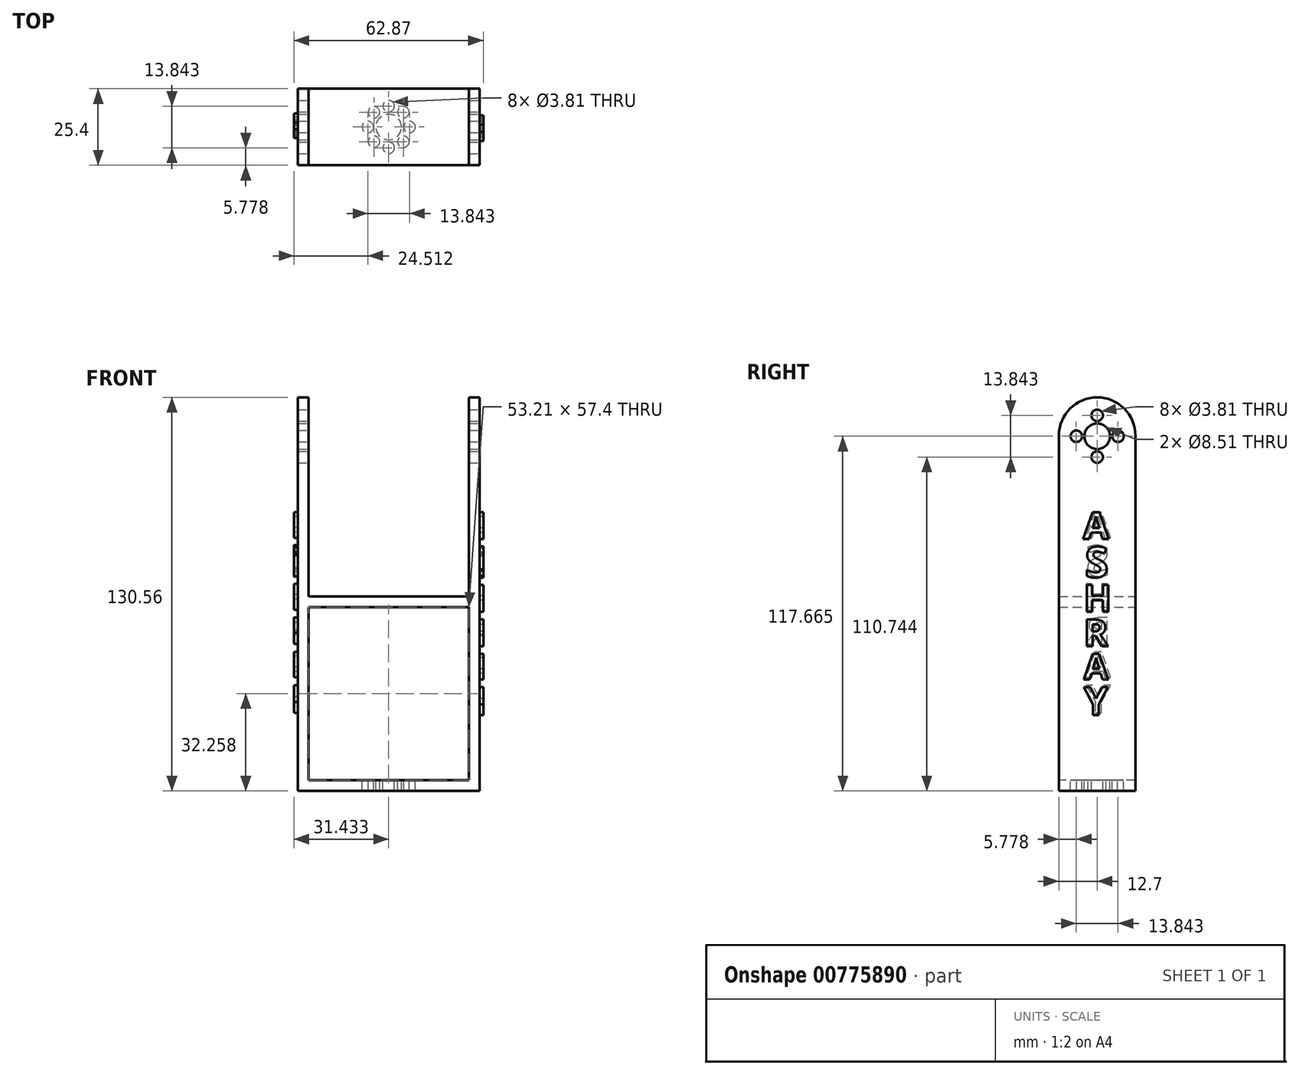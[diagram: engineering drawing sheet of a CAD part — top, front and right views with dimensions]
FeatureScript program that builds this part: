
annotation { "Feature Type Name" : "Feature", "Feature Type Description" : "" }
export const myFeature = defineFeature(function(context is Context, id is Id, definition is map)
    precondition{}
    {
        {
            var Q0;
            Q0=qCreatedBy(makeId("Top.planeOp"),FACE);
            var sketch = newSketch(context, id + "F0", { "sketchPlane" : qUnion([Q0])});
            skLineSegment(sketch, "E0.bottom", {"start": v(-26.29, 12.7) * mm, "end": v(34.04, 12.7) * mm});
            skLineSegment(sketch, "E0.top", {"start": v(-26.29, -12.7) * mm, "end": v(34.04, -12.7) * mm});
            skLineSegment(sketch, "E0.left", {"start": v(-26.29, 12.7) * mm, "end": v(-26.29, -12.7) * mm});
            skLineSegment(sketch, "E0.right", {"start": v(34.04, 12.7) * mm, "end": v(34.04, -12.7) * mm});
            skSolve(sketch);
        }
        {
            var Q0;
            Q0=makeQuery(id+"F0.imprint","IMPRINT",FACE,{"disambiguationData":[TD([[makeQuery(id+"F0.imprint","IMPRINT",EDGE,{"derivedFrom":sQuery(id+"F0.wireOp",EDGE,"E0.bottom")}),-1.0]])]});
            extrude(context, id + "F1", {"entities" : qUnion([Q0]), "depth" : 3.56 * mm});
        }
        {
            var Q0;
            Q0=makeQuery(id+"F1.opExtrude","CAP_FACE",FACE,{"disambiguationData":[OSD([sQuery(id+"F0.wireOp",EDGE,"E0.bottom"),sQuery(id+"F0.wireOp",EDGE,"E0.top"),sQuery(id+"F0.wireOp",EDGE,"E0.left"),sQuery(id+"F0.wireOp",EDGE,"E0.right")])],"isStart":false});
            var sketch = newSketch(context, id + "F2", { "sketchPlane" : qUnion([Q0])});
            skLineSegment(sketch, "E1.bottom", {"start": v(-26.29, 12.7) * mm, "end": v(-22.73, 12.7) * mm});
            skLineSegment(sketch, "E1.top", {"start": v(-26.29, -12.7) * mm, "end": v(-22.73, -12.7) * mm});
            skLineSegment(sketch, "E1.left", {"start": v(-26.29, 12.7) * mm, "end": v(-26.29, -12.7) * mm});
            skLineSegment(sketch, "E1.right", {"start": v(-22.73, 12.7) * mm, "end": v(-22.73, -12.7) * mm});
            skLineSegment(sketch, "E2.bottom", {"start": v(34.04, 12.7) * mm, "end": v(30.48, 12.7) * mm});
            skLineSegment(sketch, "E2.top", {"start": v(34.04, -12.7) * mm, "end": v(30.48, -12.7) * mm});
            skLineSegment(sketch, "E2.left", {"start": v(34.04, 12.7) * mm, "end": v(34.04, -12.7) * mm});
            skLineSegment(sketch, "E2.right", {"start": v(30.48, 12.7) * mm, "end": v(30.48, -12.7) * mm});
            skSolve(sketch);
        }
        {
            var Q0;
            Q0=makeQuery(id+"F2.imprint","IMPRINT",FACE,{"disambiguationData":[TD([[makeQuery(id+"F2.imprint","IMPRINT",EDGE,{"derivedFrom":sQuery(id+"F2.wireOp",EDGE,"E1.bottom")}),-1.0]])]});
            var Q1;
            Q1=makeQuery(id+"F2.imprint","IMPRINT",FACE,{"disambiguationData":[TD([[makeQuery(id+"F2.imprint","IMPRINT",EDGE,{"derivedFrom":sQuery(id+"F2.wireOp",EDGE,"E2.bottom")}),-1.0]])]});
            extrude(context, id + "F3", {"entities" : qUnion([Q0, Q1]), "operationType" : NewBodyOperationType.ADD, "depth" : 127 * mm});
        }
        {
            var Q0;
            Q0=makeQuery(id+"F3.opExtrude","CAP_EDGE",EDGE,{"disambiguationData":[OSD([sQuery(id+"F2.wireOp",EDGE,"E2.bottom")])],"isStart":false});
            fillet(context, id + "F4", {"entities" : qUnion([Q0]), "radius" : 12.7 * mm, "tangentPropagation" : true, "allowEdgeOverflow" : false});
        }
        {
            var Q0;
            Q0=makeQuery(id+"F3.opExtrude","CAP_EDGE",EDGE,{"disambiguationData":[OSD([sQuery(id+"F2.wireOp",EDGE,"E2.top")])],"isStart":false});
            var Q1;
            Q1=makeQuery(id+"F3.opExtrude","CAP_EDGE",EDGE,{"disambiguationData":[OSD([sQuery(id+"F2.wireOp",EDGE,"E1.top")])],"isStart":false});
            var Q2;
            Q2=makeQuery(id+"F3.opExtrude","CAP_EDGE",EDGE,{"disambiguationData":[OSD([sQuery(id+"F2.wireOp",EDGE,"E1.bottom")])],"isStart":false});
            fillet(context, id + "F5", {"entities" : qUnion([Q0, Q1, Q2]), "radius" : 12.7 * mm, "tangentPropagation" : true, "allowEdgeOverflow" : false});
        }
        {
            var Q0;
            Q0=makeQuery(id+"F3.boolean.opBoolean","MERGE",FACE,{"derivedFrom":[makeQuery(id+"F1.opExtrude","SWEPT_FACE",FACE,{"disambiguationData":[OSD([sQuery(id+"F0.wireOp",EDGE,"E0.right")])]}),makeQuery(id+"F3.opExtrude","SWEPT_FACE",FACE,{"disambiguationData":[OSD([sQuery(id+"F2.wireOp",EDGE,"E2.left")])]})]});
            var sketch = newSketch(context, id + "F6", { "sketchPlane" : qUnion([Q0])});
            skCircle(sketch, "E3", {"center": v(0, 124.59) * mm, "radius": 1.9 * mm});
            skCircle(sketch, "E4", {"center": v(0, 110.74) * mm, "radius": 1.9 * mm});
            skCircle(sketch, "E5", {"center": v(0, 117.67) * mm, "radius": 4.25 * mm});
            skCircle(sketch, "E6", {"center": v(6.92, 117.67) * mm, "radius": 1.9 * mm});
            skCircle(sketch, "E7", {"center": v(-6.92, 117.67) * mm, "radius": 1.9 * mm});
            skSolve(sketch);
        }
        {
            var Q0;
            Q0=makeQuery(id+"F6.imprint","IMPRINT",FACE,{"disambiguationData":[TD([[makeQuery(id+"F6.imprint","IMPRINT",EDGE,{"derivedFrom":sQuery(id+"F6.wireOp",EDGE,"E5")}),1.0]])]});
            var Q1;
            Q1=makeQuery(id+"F6.imprint","IMPRINT",FACE,{"disambiguationData":[TD([[makeQuery(id+"F6.imprint","IMPRINT",EDGE,{"derivedFrom":sQuery(id+"F6.wireOp",EDGE,"E3")}),1.0]])]});
            var Q2;
            Q2=makeQuery(id+"F6.imprint","IMPRINT",FACE,{"disambiguationData":[TD([[makeQuery(id+"F6.imprint","IMPRINT",EDGE,{"derivedFrom":sQuery(id+"F6.wireOp",EDGE,"E7")}),1.0]])]});
            var Q3;
            Q3=makeQuery(id+"F6.imprint","IMPRINT",FACE,{"disambiguationData":[TD([[makeQuery(id+"F6.imprint","IMPRINT",EDGE,{"derivedFrom":sQuery(id+"F6.wireOp",EDGE,"E4")}),1.0]])]});
            var Q4;
            Q4=makeQuery(id+"F6.imprint","IMPRINT",FACE,{"disambiguationData":[TD([[makeQuery(id+"F6.imprint","IMPRINT",EDGE,{"derivedFrom":sQuery(id+"F6.wireOp",EDGE,"E6")}),1.0]])]});
            extrude(context, id + "F7", {"entities" : qUnion([Q0, Q1, Q2, Q3, Q4]), "operationType" : NewBodyOperationType.REMOVE, "oppositeDirection" : true, "depth" : 254 * mm});
        }
        {
            var Q0;
            Q0=makeQuery(id+"F1.opExtrude","CAP_FACE",FACE,{"disambiguationData":[OSD([sQuery(id+"F0.wireOp",EDGE,"E0.bottom"),sQuery(id+"F0.wireOp",EDGE,"E0.top"),sQuery(id+"F0.wireOp",EDGE,"E0.left"),sQuery(id+"F0.wireOp",EDGE,"E0.right")])],"isStart":false});
            var sketch = newSketch(context, id + "F8", { "sketchPlane" : qUnion([Q0])});
            skCircle(sketch, "E8", {"center": v(3.87, 0) * mm, "radius": 4.25 * mm});
            skCircle(sketch, "E9", {"center": v(3.87, 6.92) * mm, "radius": 1.9 * mm});
            skCircle(sketch, "E10", {"center": v(10.8, 0) * mm, "radius": 1.9 * mm});
            skCircle(sketch, "E11", {"center": v(3.87, -6.92) * mm, "radius": 1.9 * mm});
            skCircle(sketch, "E12", {"center": v(-3.05, 0) * mm, "radius": 1.9 * mm});
            skCircle(sketch, "E13", {"center": v(-1.02, -4.9) * mm, "radius": 1.9 * mm});
            skCircle(sketch, "E14", {"center": v(8.77, -4.9) * mm, "radius": 1.9 * mm});
            skCircle(sketch, "E15", {"center": v(8.77, 4.9) * mm, "radius": 1.9 * mm});
            skCircle(sketch, "E16", {"center": v(-1.02, 4.9) * mm, "radius": 1.9 * mm});
            skLineSegment(sketch, "E17", {"start": v(-1.02, -4.9) * mm, "end": v(3.87, 0) * mm});
            skLineSegment(sketch, "E18", {"start": v(3.87, 0) * mm, "end": v(8.77, -4.9) * mm});
            skLineSegment(sketch, "E19", {"start": v(3.87, 0) * mm, "end": v(8.77, 4.9) * mm});
            skLineSegment(sketch, "E20", {"start": v(3.87, 0) * mm, "end": v(-1.02, 4.9) * mm});
            skSolve(sketch);
        }
        {
            var Q0;
            Q0=makeQuery(id+"F3.opExtrude","SWEPT_FACE",FACE,{"disambiguationData":[OSD([sQuery(id+"F2.wireOp",EDGE,"E2.right")])]});
            var sketch = newSketch(context, id + "F9", { "sketchPlane" : qUnion([Q0])});
            skLineSegment(sketch, "E21.bottom", {"start": v(12.7, 64.52) * mm, "end": v(-12.7, 64.52) * mm});
            skLineSegment(sketch, "E21.top", {"start": v(12.7, 60.96) * mm, "end": v(-12.7, 60.96) * mm});
            skLineSegment(sketch, "E21.left", {"start": v(12.7, 64.52) * mm, "end": v(12.7, 60.96) * mm});
            skLineSegment(sketch, "E21.right", {"start": v(-12.7, 64.52) * mm, "end": v(-12.7, 60.96) * mm});
            skSolve(sketch);
        }
        {
            var Q0;
            Q0=makeQuery(id+"F3.boolean.opBoolean","MERGE",FACE,{"derivedFrom":[makeQuery(id+"F1.opExtrude","SWEPT_FACE",FACE,{"disambiguationData":[OSD([sQuery(id+"F0.wireOp",EDGE,"E0.left")])]}),makeQuery(id+"F3.opExtrude","SWEPT_FACE",FACE,{"disambiguationData":[OSD([sQuery(id+"F2.wireOp",EDGE,"E1.left")])]})]});
            var sketch = newSketch(context, id + "F10", { "sketchPlane" : qUnion([Q0])});
            skText(sketch, "E22", { "text": "A", "fontName": "OpenSans-Bold.ttf"});
            skText(sketch, "E23", { "text": "H", "fontName": "OpenSans-Bold.ttf"});
            skText(sketch, "E24", { "text": "R", "fontName": "OpenSans-Bold.ttf"});
            skText(sketch, "E25", { "text": "A", "fontName": "OpenSans-Bold.ttf"});
            skText(sketch, "E26", { "text": "Y", "fontName": "OpenSans-Bold.ttf"});
            skText(sketch, "E27", { "text": "S", "fontName": "OpenSans-Bold.ttf"});
            const initialGuessF10  = {"E22": [-0.00444, 0.08398, 1, 0, 0.00848], "E23": [-0.00444, 0.06008, 1, 0, 0.00865], "E24": [-0.00444, 0.04872, 1, 0, 0.00883], "E25": [-0.00444, 0.0377, 1, 0, 0.00848], "E26": [-0.00444, 0.02587, 1, 0, 0.0093], "E27": [-0.00406, 0.07128, 1, 0, 0.01016]};
            skSetInitialGuess(sketch, initialGuessF10);
            skSolve(sketch);
        }
        {
            var Q0;
            Q0=makeQuery(id+"F10.imprint","IMPRINT",FACE,{"disambiguationData":[TD([[makeQuery(id+"F10.imprint","IMPRINT",EDGE,{"derivedFrom":sQuery(id+"F10.wireOp",EDGE,"E22.sketch_text.stroke-0")}),-1.0]])]});
            var Q1;
            Q1=makeQuery(id+"F10.imprint","IMPRINT",FACE,{"disambiguationData":[TD([[makeQuery(id+"F10.imprint","IMPRINT",EDGE,{"derivedFrom":sQuery(id+"F10.wireOp",EDGE,"E27.sketch_text.stroke-0")}),-1.0]])]});
            var Q2;
            Q2=makeQuery(id+"F10.imprint","IMPRINT",FACE,{"disambiguationData":[TD([[makeQuery(id+"F10.imprint","IMPRINT",EDGE,{"derivedFrom":sQuery(id+"F10.wireOp",EDGE,"E23.sketch_text.stroke-0")}),-1.0]])]});
            var Q3;
            Q3=makeQuery(id+"F10.imprint","IMPRINT",FACE,{"disambiguationData":[TD([[makeQuery(id+"F10.imprint","IMPRINT",EDGE,{"derivedFrom":sQuery(id+"F10.wireOp",EDGE,"E24.sketch_text.stroke-0")}),-1.0]])]});
            var Q4;
            Q4=makeQuery(id+"F10.imprint","IMPRINT",FACE,{"disambiguationData":[TD([[makeQuery(id+"F10.imprint","IMPRINT",EDGE,{"derivedFrom":sQuery(id+"F10.wireOp",EDGE,"E25.sketch_text.stroke-0")}),-1.0]])]});
            var Q5;
            Q5=makeQuery(id+"F10.imprint","IMPRINT",FACE,{"disambiguationData":[TD([[makeQuery(id+"F10.imprint","IMPRINT",EDGE,{"derivedFrom":sQuery(id+"F10.wireOp",EDGE,"E26.sketch_text.stroke-0")}),-1.0]])]});
            extrude(context, id + "F11", {"entities" : qUnion([Q0, Q1, Q2, Q3, Q4, Q5]), "operationType" : NewBodyOperationType.ADD, "depth" : 1.27 * mm});
        }
        {
            var Q0;
            Q0=makeQuery(id+"FYo4dK7PWjSjNg0_1.boolean.opBoolean","SPLIT",FACE,{"disambiguationData":[TD([makeQuery(id+"FYo4dK7PWjSjNg0_1.opExtrude","SWEPT_FACE",FACE,{"disambiguationData":[OSD([sQuery(id+"F9.wireOp",EDGE,"E21.top")])]})])],"derivedFrom":makeQuery(id+"F3.opExtrude","SWEPT_FACE",FACE,{"disambiguationData":[OSD([sQuery(id+"F2.wireOp",EDGE,"E1.right")])]})});
            var sketch = newSketch(context, id + "F12", { "sketchPlane" : qUnion([Q0])});
            skLineSegment(sketch, "E28.bottom", {"start": v(12.7, 45.21) * mm, "end": v(-12.7, 45.21) * mm});
            skLineSegment(sketch, "E28.top", {"start": v(12.7, 41.66) * mm, "end": v(-12.7, 41.66) * mm});
            skLineSegment(sketch, "E28.left", {"start": v(12.7, 45.21) * mm, "end": v(12.7, 41.66) * mm});
            skLineSegment(sketch, "E28.right", {"start": v(-12.7, 45.21) * mm, "end": v(-12.7, 41.66) * mm});
            skSolve(sketch);
        }
        {
            var Q0;
            Q0=makeQuery(id+"F8.imprint","IMPRINT",FACE,{"disambiguationData":[TD([[makeQuery(id+"F8.imprint","IMPRINT",EDGE,{"derivedFrom":sQuery(id+"F8.wireOp",EDGE,"E15")}),1.0]])]});
            var Q1;
            Q1=makeQuery(id+"F8.imprint","IMPRINT",FACE,{"disambiguationData":[TD([[makeQuery(id+"F8.imprint","IMPRINT",EDGE,{"derivedFrom":sQuery(id+"F8.wireOp",EDGE,"E10")}),1.0]])]});
            var Q2;
            Q2=makeQuery(id+"F8.imprint","IMPRINT",FACE,{"disambiguationData":[TD([[makeQuery(id+"F8.imprint","IMPRINT",EDGE,{"derivedFrom":sQuery(id+"F8.wireOp",EDGE,"E14")}),1.0]])]});
            var Q3;
            Q3=makeQuery(id+"F8.imprint","IMPRINT",FACE,{"disambiguationData":[TD([[makeQuery(id+"F8.imprint","IMPRINT",EDGE,{"derivedFrom":sQuery(id+"F8.wireOp",EDGE,"E11")}),1.0]])]});
            var Q4;
            Q4=makeQuery(id+"F8.imprint","IMPRINT",FACE,{"disambiguationData":[TD([[makeQuery(id+"F8.imprint","IMPRINT",EDGE,{"derivedFrom":sQuery(id+"F8.wireOp",EDGE,"E13")}),1.0]])]});
            var Q5;
            Q5=makeQuery(id+"F8.imprint","IMPRINT",FACE,{"disambiguationData":[TD([[makeQuery(id+"F8.imprint","IMPRINT",EDGE,{"derivedFrom":sQuery(id+"F8.wireOp",EDGE,"E12")}),1.0]])]});
            var Q6;
            Q6=makeQuery(id+"F8.imprint","IMPRINT",FACE,{"disambiguationData":[TD([[makeQuery(id+"F8.imprint","IMPRINT",EDGE,{"derivedFrom":sQuery(id+"F8.wireOp",EDGE,"E16")}),1.0]])]});
            var Q7;
            Q7=makeQuery(id+"F8.imprint","IMPRINT",FACE,{"disambiguationData":[TD([[makeQuery(id+"F8.imprint","IMPRINT",EDGE,{"derivedFrom":sQuery(id+"F8.wireOp",EDGE,"E9")}),1.0]])]});
            var Q8;
            {var subQ0=sQuery(id+"F8.wireOp",EDGE,"E20");var subQ1=sQuery(id+"F8.wireOp",EDGE,"E8");var subQ2=makeQuery(id+"F8.imprint","INTERSECT",VERTEX,{"derivedFrom":[subQ1,subQ0]});Q8=makeQuery(id+"F8.imprint","IMPRINT",FACE,{"disambiguationData":[TD([[makeQuery(id+"F8.imprint","IMPRINT",EDGE,{"disambiguationData":[TD([[subQ2,1.0]])],"derivedFrom":subQ1}),1.0]])]});}
            var Q9;
            {var subQ0=sQuery(id+"F8.wireOp",EDGE,"E20");var subQ1=sQuery(id+"F8.wireOp",EDGE,"E8");var subQ2=makeQuery(id+"F8.imprint","INTERSECT",VERTEX,{"derivedFrom":[subQ1,subQ0]});Q9=makeQuery(id+"F8.imprint","IMPRINT",FACE,{"disambiguationData":[TD([[makeQuery(id+"F8.imprint","IMPRINT",EDGE,{"disambiguationData":[TD([[subQ2,-1.0]])],"derivedFrom":subQ1}),1.0]])]});}
            var Q10;
            {var subQ0=sQuery(id+"F8.wireOp",EDGE,"E17");var subQ1=sQuery(id+"F8.wireOp",EDGE,"E8");var subQ2=makeQuery(id+"F8.imprint","INTERSECT",VERTEX,{"derivedFrom":[subQ1,subQ0]});Q10=makeQuery(id+"F8.imprint","IMPRINT",FACE,{"disambiguationData":[TD([[makeQuery(id+"F8.imprint","IMPRINT",EDGE,{"disambiguationData":[TD([[subQ2,-1.0]])],"derivedFrom":subQ1}),1.0]])]});}
            var Q11;
            {var subQ0=sQuery(id+"F8.wireOp",EDGE,"E19");var subQ1=sQuery(id+"F8.wireOp",EDGE,"E8");var subQ2=makeQuery(id+"F8.imprint","INTERSECT",VERTEX,{"derivedFrom":[subQ1,subQ0]});Q11=makeQuery(id+"F8.imprint","IMPRINT",FACE,{"disambiguationData":[TD([[makeQuery(id+"F8.imprint","IMPRINT",EDGE,{"disambiguationData":[TD([[subQ2,1.0]])],"derivedFrom":subQ1}),1.0]])]});}
            extrude(context, id + "F13", {"entities" : qUnion([Q0, Q1, Q2, Q3, Q4, Q5, Q6, Q7, Q8, Q9, Q10, Q11]), "operationType" : NewBodyOperationType.REMOVE, "oppositeDirection" : true, "depth" : 25.4 * mm});
        }
        {
            var Q0;
            Q0=makeQuery(id+"F3.boolean.opBoolean","MERGE",FACE,{"derivedFrom":[makeQuery(id+"F1.opExtrude","SWEPT_FACE",FACE,{"disambiguationData":[OSD([sQuery(id+"F0.wireOp",EDGE,"E0.right")])]}),makeQuery(id+"F3.opExtrude","SWEPT_FACE",FACE,{"disambiguationData":[OSD([sQuery(id+"F2.wireOp",EDGE,"E2.left")])]})]});
            var sketch = newSketch(context, id + "F14", { "sketchPlane" : qUnion([Q0])});
            skText(sketch, "E29", { "text": "A", "fontName": "OpenSans-Bold.ttf"});
            skText(sketch, "E30", { "text": "S", "fontName": "OpenSans-Bold.ttf"});
            skText(sketch, "E31", { "text": "H", "fontName": "OpenSans-Bold.ttf"});
            skText(sketch, "E32", { "text": "R", "fontName": "OpenSans-Bold.ttf"});
            skText(sketch, "E33", { "text": "A", "fontName": "OpenSans-Bold.ttf"});
            skText(sketch, "E34", { "text": "Y", "fontName": "OpenSans-Bold.ttf"});
            const initialGuessF14  = {"E29": [-0.00466, 0.08357, 1, 0, 0.0089], "E30": [-0.00406, 0.07087, 1, 0, 0.01016], "E31": [-0.00457, 0.05944, 1, 0, 0.0089], "E32": [-0.00448, 0.048, 1, 0, 0.0089], "E33": [-0.00444, 0.03699, 1, 0, 0.00848], "E34": [-0.00444, 0.02516, 1, 0, 0.0093]};
            skSetInitialGuess(sketch, initialGuessF14);
            skSolve(sketch);
        }
        {
            var Q0;
            Q0=makeQuery(id+"F14.imprint","IMPRINT",FACE,{"disambiguationData":[TD([[makeQuery(id+"F14.imprint","IMPRINT",EDGE,{"derivedFrom":sQuery(id+"F14.wireOp",EDGE,"E29.sketch_text.stroke-0")}),-1.0]])]});
            var Q1;
            Q1=makeQuery(id+"F14.imprint","IMPRINT",FACE,{"disambiguationData":[TD([[makeQuery(id+"F14.imprint","IMPRINT",EDGE,{"derivedFrom":sQuery(id+"F14.wireOp",EDGE,"E30.sketch_text.stroke-0")}),-1.0]])]});
            var Q2;
            Q2=makeQuery(id+"F14.imprint","IMPRINT",FACE,{"disambiguationData":[TD([[makeQuery(id+"F14.imprint","IMPRINT",EDGE,{"derivedFrom":sQuery(id+"F14.wireOp",EDGE,"E31.sketch_text.stroke-0")}),-1.0]])]});
            var Q3;
            Q3=makeQuery(id+"F14.imprint","IMPRINT",FACE,{"disambiguationData":[TD([[makeQuery(id+"F14.imprint","IMPRINT",EDGE,{"derivedFrom":sQuery(id+"F14.wireOp",EDGE,"E32.sketch_text.stroke-0")}),-1.0]])]});
            var Q4;
            Q4=makeQuery(id+"F14.imprint","IMPRINT",FACE,{"disambiguationData":[TD([[makeQuery(id+"F14.imprint","IMPRINT",EDGE,{"derivedFrom":sQuery(id+"F14.wireOp",EDGE,"E33.sketch_text.stroke-0")}),-1.0]])]});
            var Q5;
            Q5=makeQuery(id+"F14.imprint","IMPRINT",FACE,{"disambiguationData":[TD([[makeQuery(id+"F14.imprint","IMPRINT",EDGE,{"derivedFrom":sQuery(id+"F14.wireOp",EDGE,"E34.sketch_text.stroke-0")}),-1.0]])]});
            extrude(context, id + "F15", {"entities" : qUnion([Q0, Q1, Q2, Q3, Q4, Q5]), "operationType" : NewBodyOperationType.ADD, "depth" : 1.27 * mm});
        }
        {
            var Q0;
            Q0=makeQuery(id+"F9.imprint","IMPRINT",FACE,{"disambiguationData":[TD([[makeQuery(id+"F9.imprint","IMPRINT",EDGE,{"derivedFrom":sQuery(id+"F9.wireOp",EDGE,"E21.bottom")}),1.0]])]});
            extrude(context, id + "F16", {"entities" : qUnion([Q0]), "operationType" : NewBodyOperationType.ADD, "depth" : 53.34 * mm});
        }
    });
